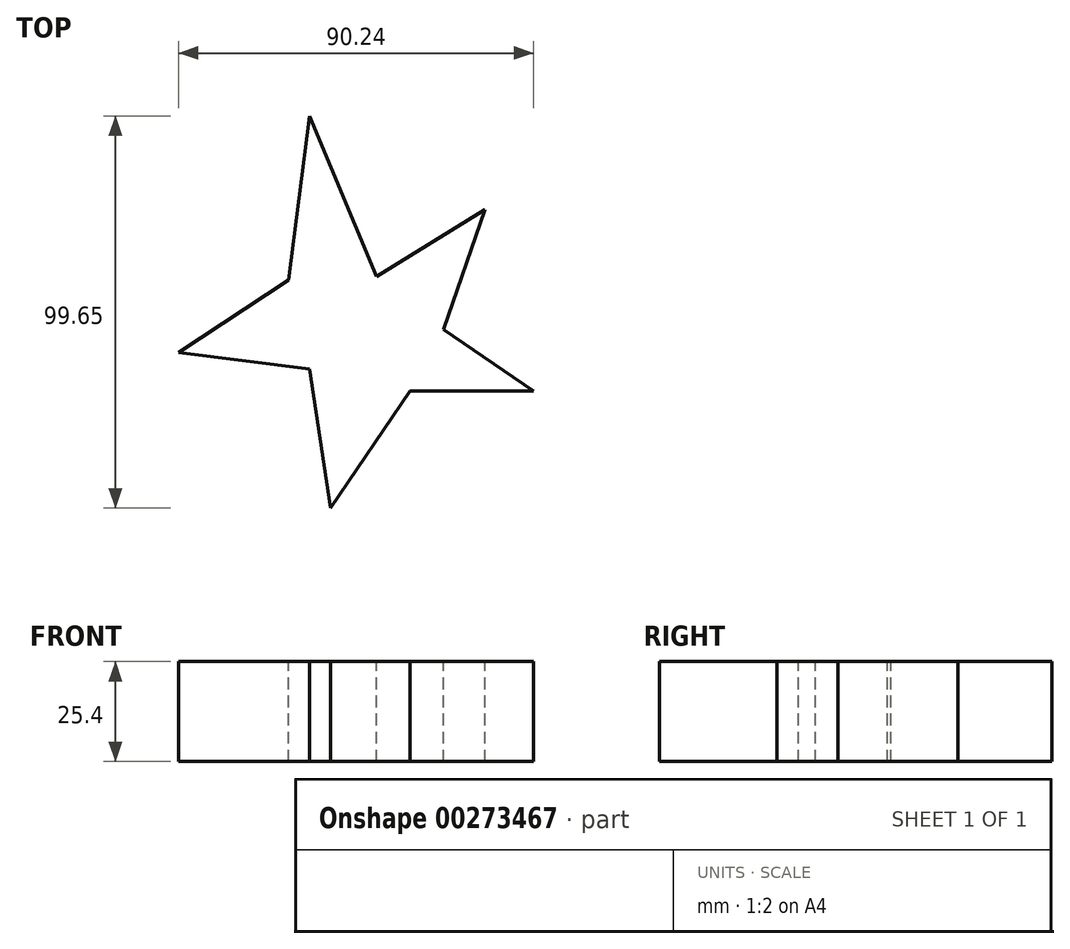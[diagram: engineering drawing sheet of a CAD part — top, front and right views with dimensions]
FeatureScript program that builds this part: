
annotation { "Feature Type Name" : "Feature", "Feature Type Description" : "" }
export const myFeature = defineFeature(function(context is Context, id is Id, definition is map)
    precondition{}
    {
        {
            var Q0;
            Q0=qCreatedBy(makeId("Top.planeOp"),FACE);
            var sketch = newSketch(context, id + "F0", { "sketchPlane" : qUnion([Q0])});
            skLineSegment(sketch, "E0", {"start": v(-34.94, 6.31) * mm, "end": v(-29.66, 48) * mm});
            skLineSegment(sketch, "E1", {"start": v(-29.66, 48) * mm, "end": v(-12.63, 7.2) * mm});
            skLineSegment(sketch, "E2", {"start": v(-12.63, 7.2) * mm, "end": v(14.97, 24.22) * mm});
            skLineSegment(sketch, "E3", {"start": v(14.97, 24.22) * mm, "end": v(4.4, -6.31) * mm});
            skLineSegment(sketch, "E4", {"start": v(4.4, -6.31) * mm, "end": v(27.3, -21.87) * mm});
            skLineSegment(sketch, "E5", {"start": v(27.3, -21.87) * mm, "end": v(-4.11, -21.87) * mm});
            skLineSegment(sketch, "E6", {"start": v(-4.11, -21.87) * mm, "end": v(-24.33, -51.64) * mm});
            skLineSegment(sketch, "E7", {"start": v(-24.33, -51.64) * mm, "end": v(-29.66, -16.3) * mm});
            skLineSegment(sketch, "E8", {"start": v(-29.66, -16.3) * mm, "end": v(-62.93, -12.08) * mm});
            skLineSegment(sketch, "E9", {"start": v(-62.93, -12.08) * mm, "end": v(-34.94, 6.31) * mm});
            skSolve(sketch);
        }
        {
            var Q0;
            Q0=makeQuery(id+"F0.imprint","IMPRINT",FACE,{"disambiguationData":[TD([[makeQuery(id+"F0.imprint","IMPRINT",EDGE,{"derivedFrom":sQuery(id+"F0.wireOp",EDGE,"E0")}),-1.0]])]});
            extrude(context, id + "F1", {"entities" : qUnion([Q0]), "oppositeDirection" : true, "depth" : 25.4 * mm});
        }
    });
